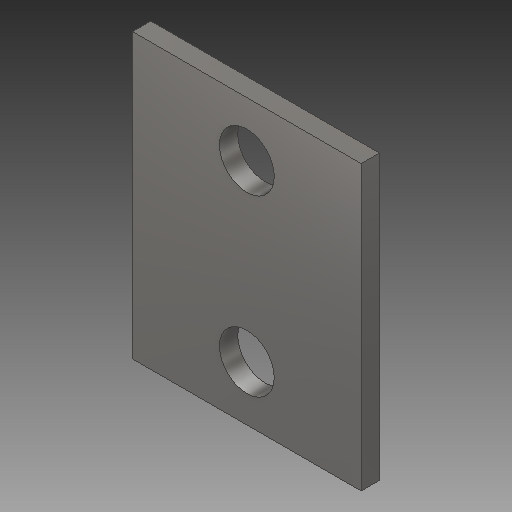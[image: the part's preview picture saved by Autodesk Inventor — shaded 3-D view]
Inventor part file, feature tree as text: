
AUTODESK INVENTOR PART (.ipt)
format: ipt  version: 2018.1 (Build 221171000, 171)  size: 117,248 bytes
history: native  units: mm
features: other x1, extrude x1, sketch x1
ambient origin geometry x8: Origin, YZ Plane, XZ Plane, XY Plane, X Axis, Y Axis, Z Axis, Center Point
bodies: Solid1 (feature_tree)
feature tree (3):
  parser-record x1  (decoder bookkeeping rows leaked as tree rows — omitted from the tree; the rows remain in map.json)
  extrude  "Extrusion1"  Depth=31.0mm
  sketch  "Sketch1"  dims[d0=25.0mm d1=31.0mm d2=6.0mm d3=19.05mm d4=2.0mm d5=0.0mm]
note: 1 file-system path scrubbed to <path> (originals preserved in map.json)
